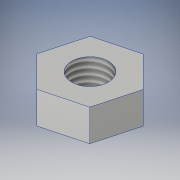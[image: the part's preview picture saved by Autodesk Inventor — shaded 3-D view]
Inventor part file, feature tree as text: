
AUTODESK INVENTOR PART (.ipt)
format: ipt  version: 2018 (Build 220112000, 112)  size: 103,424 bytes
history: native  units: in
note: dims shown in document units (in); Inventor stores cm internally (conversion verified against a paired STEP export)
features: extrude x1, thread x1, sketch x1
ambient origin geometry x8: Origin, YZ Plane, XZ Plane, XY Plane, X Axis, Y Axis, Z Axis, Center Point
bodies: Solid1 (feature_tree)
feature tree (3):
  extrude  "Extrusion1"  Depth=0.065in
  thread  "Thread1"  [1 undecoded]
  sketch  "Sketch1"  dims[d0=0.154in d1=0.075in d2=0.065in d3=0.0in d4=1.0in d5=0.0in]
note: 1 required parameter value undecoded (feature->parameter linkage not recoverable at this tier; creation-order binding heuristic only, values carry confidence <= 0.55)
